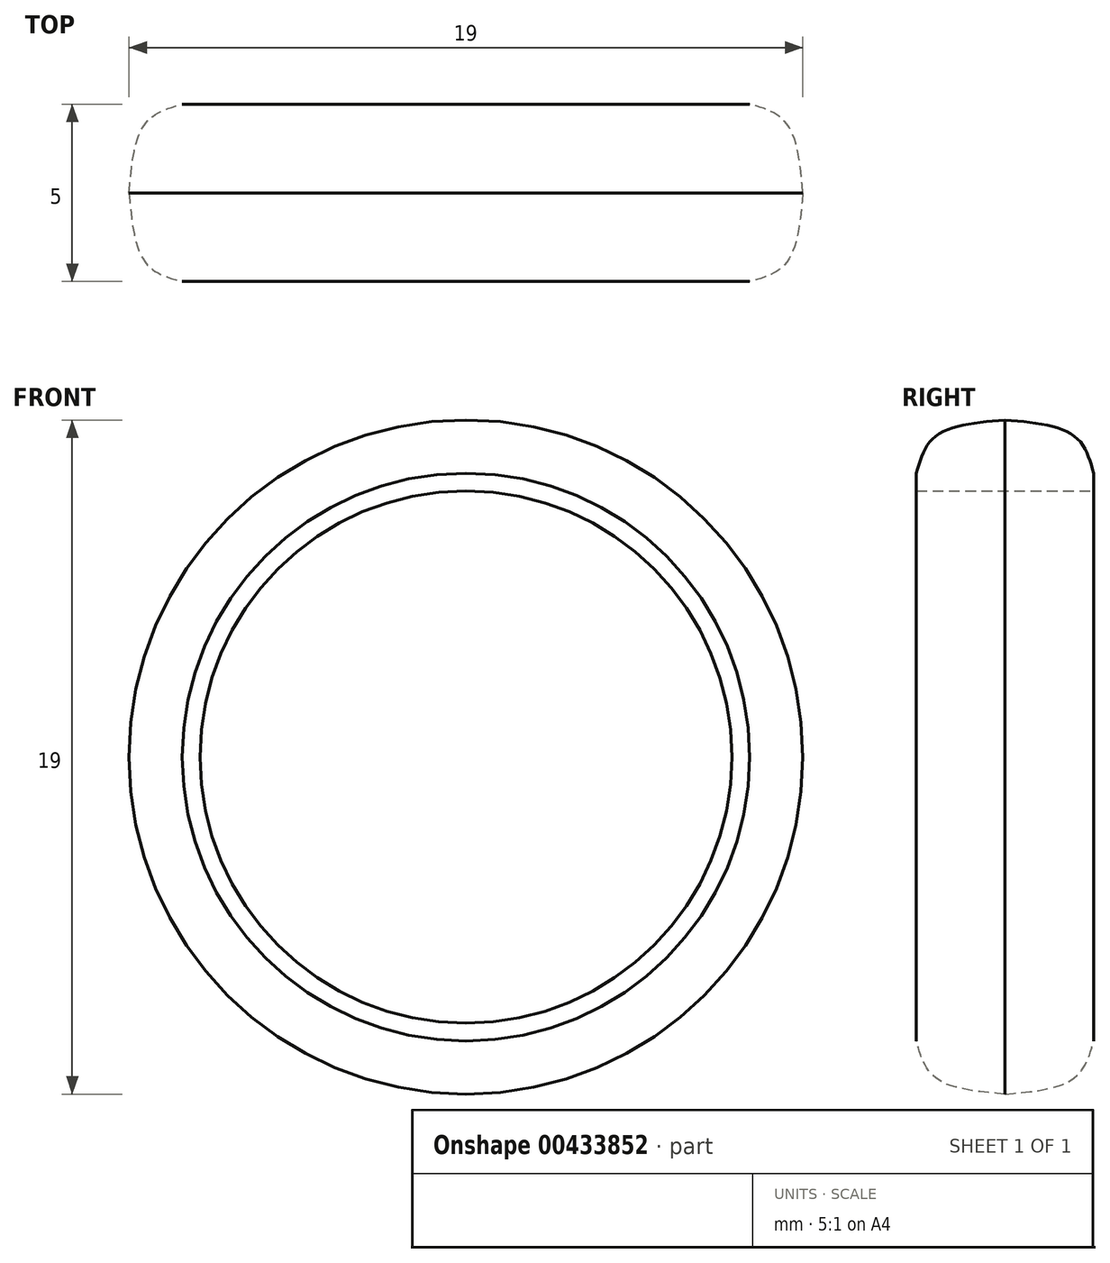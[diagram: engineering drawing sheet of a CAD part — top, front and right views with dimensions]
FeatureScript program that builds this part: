
annotation { "Feature Type Name" : "Feature", "Feature Type Description" : "" }
export const myFeature = defineFeature(function(context is Context, id is Id, definition is map)
    precondition{}
    {
        {
            var Q0;
            Q0=qCreatedBy(makeId("Right.planeOp"),FACE);
            var sketch = newSketch(context, id + "F0", { "sketchPlane" : qUnion([Q0])});
            skLineSegment(sketch, "E0", {"start": v(0, 7.5) * mm, "end": v(-2.5, 7.5) * mm});
            skLineSegment(sketch, "E1", {"start": v(-2.5, 7.5) * mm, "end": v(-2.5, 8) * mm});
            skFitSpline(sketch, "E2", {"points": [v(-2.5, 8) * mm, v(-1.96, 9.04) * mm, v(0, 9.5) * mm], "startDerivative": vector(0.77, 2.75) * mm, "endDerivative": vector(4.08, 0.36) * mm});
            skFitSpline(sketch, "E3.MirrorCS", {"points": [v(2.5, 8) * mm, v(1.96, 9.04) * mm, v(0, 9.5) * mm], "startDerivative": vector(-0.77, 2.75) * mm, "endDerivative": vector(-4.08, 0.36) * mm});
            skLineSegment(sketch, "E4.MirrorCS", {"start": v(2.5, 7.5) * mm, "end": v(2.5, 8) * mm});
            skLineSegment(sketch, "E5.MirrorCS", {"start": v(0, 7.5) * mm, "end": v(2.5, 7.5) * mm});
            skSolve(sketch);
        }
        {
            var Q0;
            Q0=qCreatedBy(makeId("Front.planeOp"),FACE);
            var sketch = newSketch(context, id + "F1", { "sketchPlane" : qUnion([Q0])});
            skCircle(sketch, "E6", {"center": v(0, 0) * mm, "radius": 7.5 * mm});
            skSolve(sketch);
        }
        {
            var Q0;
            Q0=makeQuery(id+"F0.imprint","IMPRINT",FACE,{"disambiguationData":[TD([[makeQuery(id+"F0.imprint","IMPRINT",EDGE,{"derivedFrom":sQuery(id+"F0.wireOp",EDGE,"E0")}),-1.0]])]});
            var Q1;
            Q1=sQuery(id+"F1.wireOp",EDGE,"E6");
            revolve(context, id + "F2", {"entities" : qUnion([Q0]), "axis" : qUnion([Q1]), "revolveType" : RevolveType.FULL});
        }
        {
            var Q0;
            Q0=makeQuery(id+"F2.opRevolve","SWEPT_BODY",BODY,{"disambiguationData":[OSD([sQuery(id+"F0.wireOp",EDGE,"E0"),sQuery(id+"F0.wireOp",EDGE,"E1"),sQuery(id+"F0.wireOp",EDGE,"E2"),sQuery(id+"F0.wireOp",EDGE,"E3.MirrorCS"),sQuery(id+"F0.wireOp",EDGE,"E4.MirrorCS"),sQuery(id+"F0.wireOp",EDGE,"E5.MirrorCS")])]});
            transform(context, id + "F3", {"entities" : qUnion([Q0]), "transformType" : TransformType.TRANSLATION_3D, "dx" : 0 * mm, "dy" : 0 * mm, "dz" : 0 * mm, "makeCopy" : true});
        }
    });
